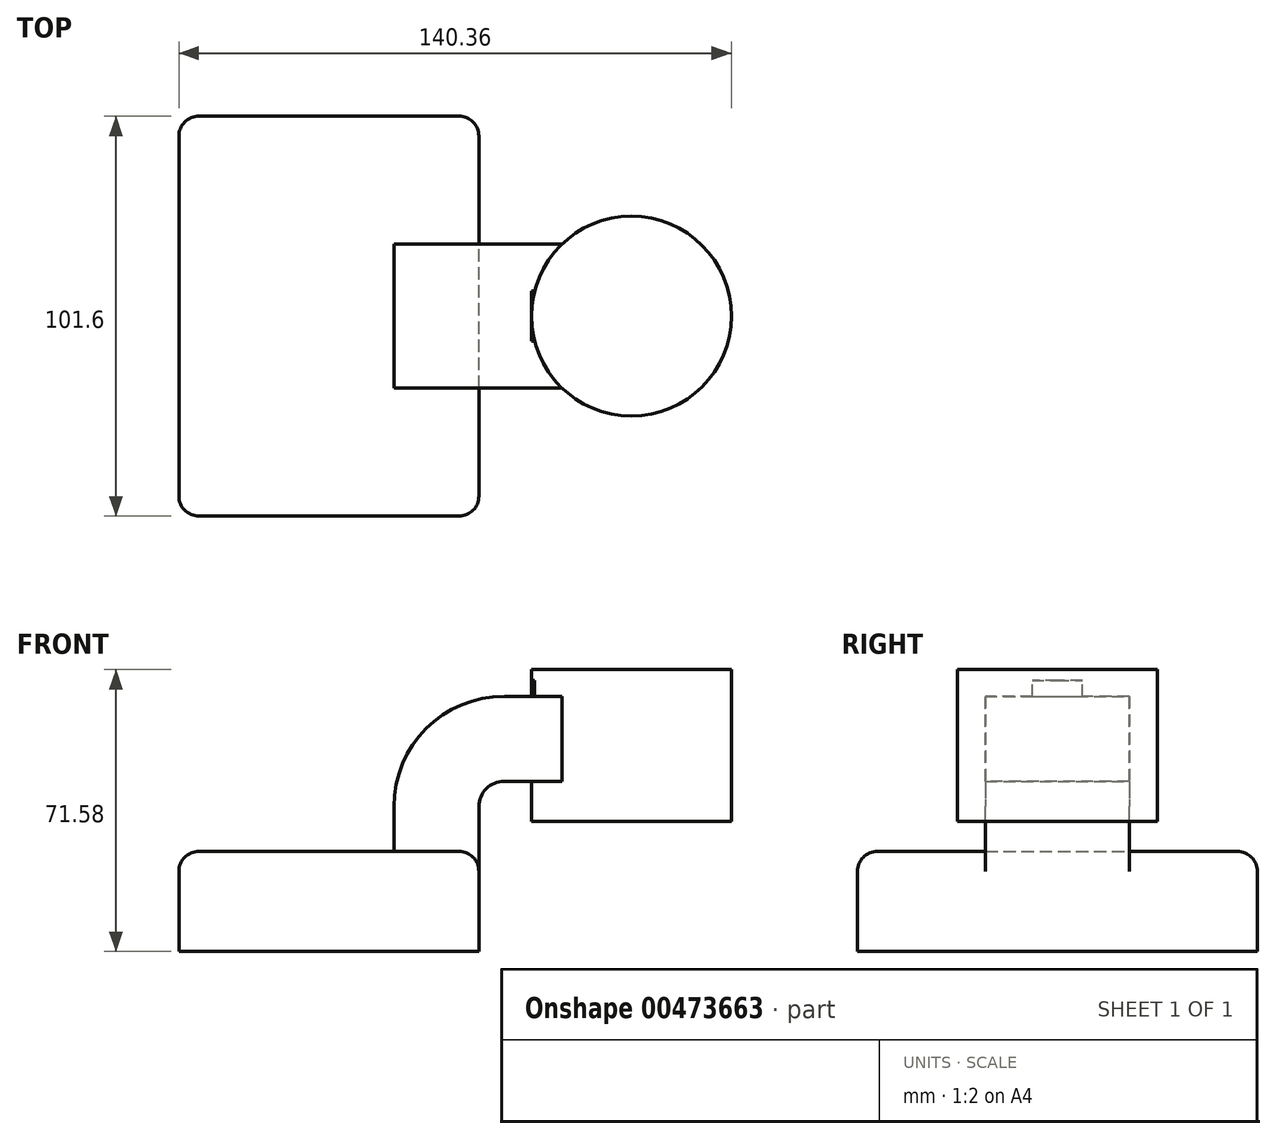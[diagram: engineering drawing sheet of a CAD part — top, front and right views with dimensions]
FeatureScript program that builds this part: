
annotation { "Feature Type Name" : "Feature", "Feature Type Description" : "" }
export const myFeature = defineFeature(function(context is Context, id is Id, definition is map)
    precondition{}
    {
        {
            var Q0;
            Q0=qCreatedBy(makeId("Front.planeOp"),FACE);
            var sketch = newSketch(context, id + "F0", { "sketchPlane" : qUnion([Q0])});
            skLineSegment(sketch, "E0.bottom", {"start": v(38.1, 12.7) * mm, "end": v(-38.1, 12.7) * mm});
            skLineSegment(sketch, "E0.top", {"start": v(38.1, -12.7) * mm, "end": v(-38.1, -12.7) * mm});
            skLineSegment(sketch, "E0.left", {"start": v(38.1, 12.7) * mm, "end": v(38.1, -12.7) * mm});
            skLineSegment(sketch, "E0.right", {"start": v(-38.1, 12.7) * mm, "end": v(-38.1, -12.7) * mm});
            skPoint(sketch, "E0.middle", {"position": v(0, 0) * mm});
            skLineSegment(sketch, "E1.bottom", {"start": v(102.26, 20.25) * mm, "end": v(51.46, 20.25) * mm});
            skLineSegment(sketch, "E1.top", {"start": v(102.26, 58.88) * mm, "end": v(51.46, 58.88) * mm});
            skLineSegment(sketch, "E1.left", {"start": v(102.26, 20.25) * mm, "end": v(102.26, 58.88) * mm});
            skLineSegment(sketch, "E1.right", {"start": v(51.46, 20.25) * mm, "end": v(51.46, 58.88) * mm});
            skPoint(sketch, "E1.middle", {"position": v(76.86, 39.56) * mm});
            skLineSegment(sketch, "E2", {"start": v(38.1, 12.7) * mm, "end": v(38.1, 24.05) * mm});
            skArc(sketch, "E3", {"start": v(38.1, 24.05) * mm, "mid": v(40, 28.62) * mm, "end": v(44.56, 30.52) * mm});
            skLineSegment(sketch, "E4", {"start": v(44.56, 30.52) * mm, "end": v(64.02, 30.52) * mm});
            skLineSegment(sketch, "E5.0", {"start": v(44.56, 52.1) * mm, "end": v(64.02, 52.1) * mm});
            skArc(sketch, "E5.1", {"start": v(16.51, 24.05) * mm, "mid": v(24.73, 43.89) * mm, "end": v(44.56, 52.1) * mm});
            skLineSegment(sketch, "E5.2", {"start": v(16.51, 12.7) * mm, "end": v(16.51, 24.05) * mm});
            skLineSegment(sketch, "E6", {"start": v(64.02, 52.1) * mm, "end": v(64.02, 30.52) * mm});
            skLineSegment(sketch, "E7", {"start": v(76.86, 58.88) * mm, "end": v(76.86, 20.25) * mm});
            skFitSpline(sketch, "E8", {"points": [v(58.44, 55.5) * mm, v(18.35, 56.1) * mm, v(-17.15, 31.6) * mm, v(-30.64, 12.7) * mm], "startDerivative": vector(-110.76, 7.8) * mm, "endDerivative": vector(-40.24, -66.62) * mm});
            skLineSegment(sketch, "E9", {"start": v(58.44, 55.5) * mm, "end": v(58.44, 52.1) * mm});
            skSolve(sketch);
        }
        {
            var Q0;
            Q0=makeQuery(id+"F0.imprint","IMPRINT",FACE,{"disambiguationData":[TD([[makeQuery(id+"F0.imprint","IMPRINT",EDGE,{"derivedFrom":sQuery(id+"F0.wireOp",EDGE,"E0.top")}),-1.0]])]});
            extrude(context, id + "F1", {"entities" : qUnion([Q0]), "endBound" : BoundingType.SYMMETRIC, "depth" : 101.6 * mm});
        }
        {
            var Q0;
            {var subQ1=sQuery(id+"F0.wireOp",EDGE,"E2");Q0=makeQuery(id+"F0.imprint","IMPRINT",FACE,{"disambiguationData":[TD([[makeQuery(id+"F0.imprint","IMPRINT",EDGE,{"derivedFrom":subQ1}),1.0]])]});}
            var Q1;
            {var subQ5=sQuery(id+"F0.wireOp",EDGE,"E6");Q1=makeQuery(id+"F0.imprint","IMPRINT",FACE,{"disambiguationData":[TD([[makeQuery(id+"F0.imprint","IMPRINT",EDGE,{"derivedFrom":subQ5}),-1.0]])]});}
            extrude(context, id + "F2", {"entities" : qUnion([Q0, Q1]), "operationType" : NewBodyOperationType.ADD, "endBound" : BoundingType.SYMMETRIC, "depth" : 36.58 * mm});
        }
        {
            var Q0;
            {var subQ0=sQuery(id+"F0.wireOp",EDGE,"E5.1");Q0=makeQuery(id+"F0.imprint","IMPRINT",FACE,{"disambiguationData":[TD([[makeQuery(id+"F0.imprint","IMPRINT",EDGE,{"derivedFrom":subQ0}),1.0]])]});}
            var Q1;
            {var subQ5=sQuery(id+"F0.wireOp",EDGE,"E9");Q1=makeQuery(id+"F0.imprint","IMPRINT",FACE,{"disambiguationData":[TD([[makeQuery(id+"F0.imprint","IMPRINT",EDGE,{"derivedFrom":subQ5}),-1.0]])]});}
            extrude(context, id + "F3", {"entities" : qUnion([Q0, Q1]), "operationType" : NewBodyOperationType.ADD, "endBound" : BoundingType.SYMMETRIC, "depth" : 12.7 * mm});
        }
        {
            var Q0;
            {var subQ0=sQuery(id+"F0.wireOp",EDGE,"E1.left");Q0=makeQuery(id+"F0.imprint","IMPRINT",FACE,{"disambiguationData":[TD([[makeQuery(id+"F0.imprint","IMPRINT",EDGE,{"derivedFrom":subQ0}),1.0]])]});}
            var Q1;
            Q1=sQuery(id+"F0.wireOp",EDGE,"E7");
            revolve(context, id + "F4", {"operationType" : NewBodyOperationType.ADD, "entities" : qUnion([Q0]), "axis" : qUnion([Q1]), "revolveType" : RevolveType.FULL});
        }
        {
            var Q0;
            Q0=makeQuery(id+"F1.opExtrude","SWEPT_EDGE",EDGE,{"disambiguationData":[OSD([sQuery(id+"F0.wireOp",EDGE,"E0.bottom"),sQuery(id+"F0.wireOp",EDGE,"E0.right")])]});
            var Q1;
            Q1=makeQuery(id+"F1.opExtrude","CAP_EDGE",EDGE,{"disambiguationData":[OSD([sQuery(id+"F0.wireOp",EDGE,"E0.bottom")])],"isStart":false});
            var Q2;
            {var subQ0=sQuery(id+"F0.wireOp",EDGE,"E2");var subQ1=sQuery(id+"F0.wireOp",EDGE,"E0.bottom");var subQ2=sQuery(id+"F0.wireOp",EDGE,"E0.left");Q2=makeQuery(id+"F2.boolean.opBoolean","SPLIT",EDGE,{"disambiguationData":[TD([makeQuery(id+"F1.opExtrude","CAP_FACE",FACE,{"disambiguationData":[OSD([subQ1,sQuery(id+"F0.wireOp",EDGE,"E0.top"),subQ2,sQuery(id+"F0.wireOp",EDGE,"E0.right")])],"isStart":false})])],"derivedFrom":makeQuery(id+"F1.opExtrude","SWEPT_EDGE",EDGE,{"disambiguationData":[OSD([subQ1,subQ2,subQ0])]})});}
            var Q3;
            Q3=makeQuery(id+"F1.opExtrude","CAP_EDGE",EDGE,{"disambiguationData":[OSD([sQuery(id+"F0.wireOp",EDGE,"E0.left")])],"isStart":false});
            var Q4;
            Q4=makeQuery(id+"F1.opExtrude","CAP_EDGE",EDGE,{"disambiguationData":[OSD([sQuery(id+"F0.wireOp",EDGE,"E0.right")])],"isStart":false});
            var Q5;
            {var subQ0=sQuery(id+"F0.wireOp",EDGE,"E2");var subQ1=sQuery(id+"F0.wireOp",EDGE,"E0.bottom");var subQ2=sQuery(id+"F0.wireOp",EDGE,"E0.left");Q5=makeQuery(id+"F2.boolean.opBoolean","SPLIT",EDGE,{"disambiguationData":[TD([makeQuery(id+"F1.opExtrude","CAP_FACE",FACE,{"disambiguationData":[OSD([subQ1,sQuery(id+"F0.wireOp",EDGE,"E0.top"),subQ2,sQuery(id+"F0.wireOp",EDGE,"E0.right")])],"isStart":true})])],"derivedFrom":makeQuery(id+"F1.opExtrude","SWEPT_EDGE",EDGE,{"disambiguationData":[OSD([subQ1,subQ2,subQ0])]})});}
            var Q6;
            Q6=makeQuery(id+"F1.opExtrude","CAP_EDGE",EDGE,{"disambiguationData":[OSD([sQuery(id+"F0.wireOp",EDGE,"E0.left")])],"isStart":true});
            var Q7;
            Q7=makeQuery(id+"F1.opExtrude","CAP_EDGE",EDGE,{"disambiguationData":[OSD([sQuery(id+"F0.wireOp",EDGE,"E0.bottom")])],"isStart":true});
            var Q8;
            Q8=makeQuery(id+"F1.opExtrude","CAP_EDGE",EDGE,{"disambiguationData":[OSD([sQuery(id+"F0.wireOp",EDGE,"E0.right")])],"isStart":true});
            fillet(context, id + "F5", {"entities" : qUnion([Q0, Q1, Q2, Q3, Q4, Q5, Q6, Q7, Q8]), "radius" : 5.08 * mm, "tangentPropagation" : true, "allowEdgeOverflow" : false});
        }
    });
